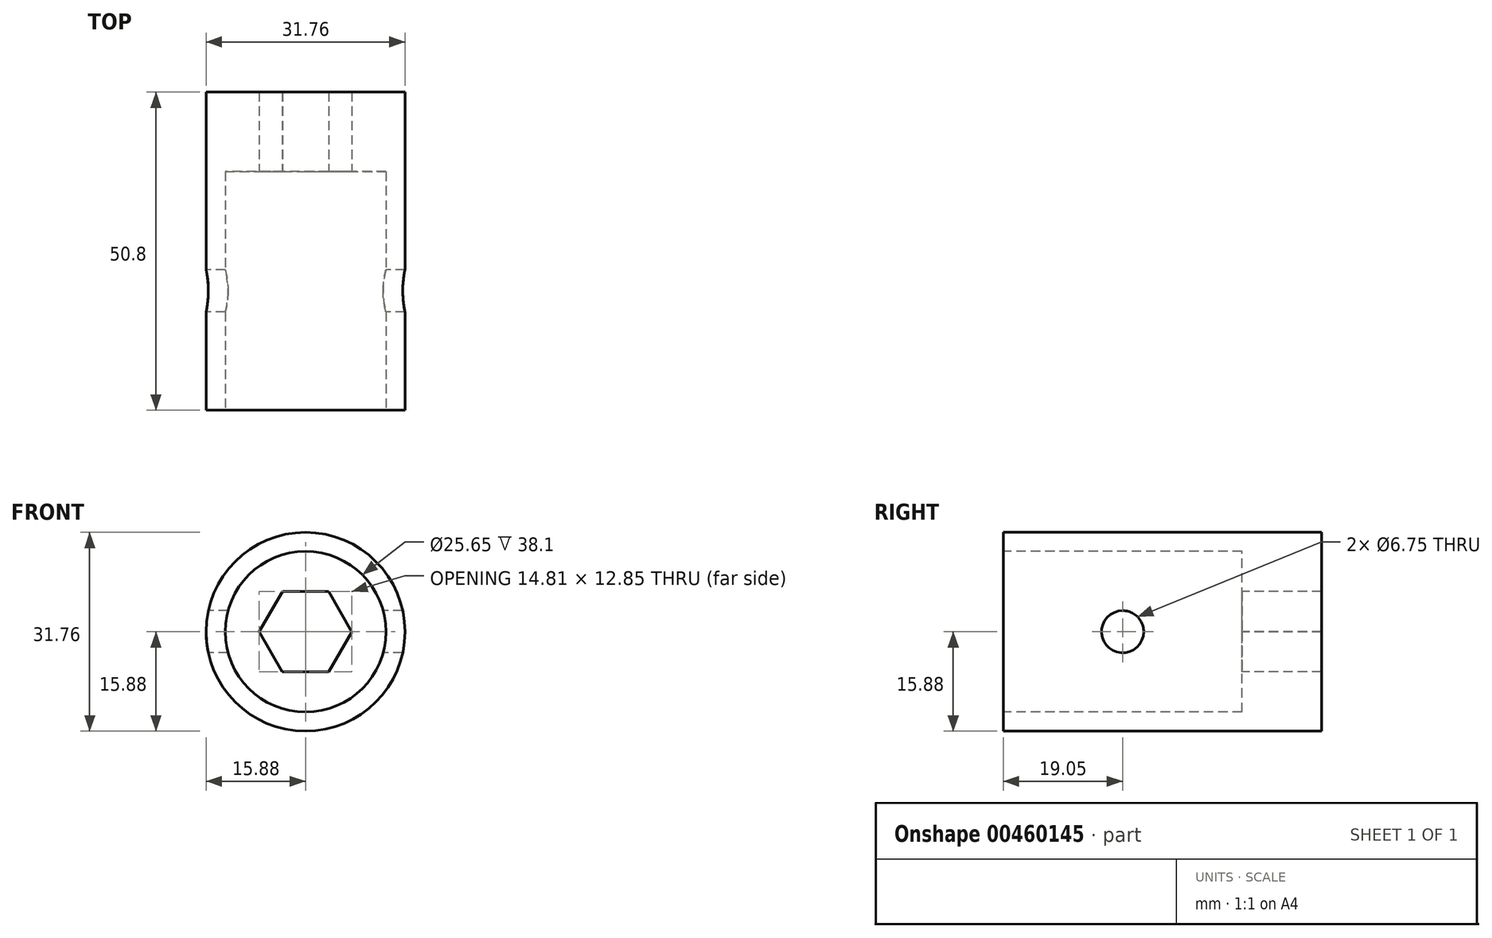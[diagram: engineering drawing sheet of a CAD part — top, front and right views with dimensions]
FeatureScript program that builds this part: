
annotation { "Feature Type Name" : "Feature", "Feature Type Description" : "" }
export const myFeature = defineFeature(function(context is Context, id is Id, definition is map)
    precondition{}
    {
        {
            var Q0;
            Q0=qCreatedBy(makeId("Front.planeOp"),FACE);
            var sketch = newSketch(context, id + "F0", { "sketchPlane" : qUnion([Q0])});
            skCircle(sketch, "E0", {"center": v(0, 0) * mm, "radius": 15.88 * mm});
            skSolve(sketch);
        }
        {
            var Q0;
            Q0=makeQuery(id+"F0.imprint","IMPRINT",FACE,{"disambiguationData":[TD([[makeQuery(id+"F0.imprint","IMPRINT",EDGE,{"derivedFrom":sQuery(id+"F0.wireOp",EDGE,"E0")}),1.0]])]});
            extrude(context, id + "F1", {"entities" : qUnion([Q0]), "depth" : 50.8 * mm, "offsetDistance" : 25.4 * mm});
        }
        {
            var Q0;
            Q0=makeQuery(id+"F1.opExtrude","CAP_FACE",FACE,{"disambiguationData":[OSD([sQuery(id+"F0.wireOp",EDGE,"E0")])],"isStart":false});
            var sketch = newSketch(context, id + "F2", { "sketchPlane" : qUnion([Q0])});
            skCircle(sketch, "E1", {"center": v(0, 0) * mm, "radius": 12.83 * mm});
            skSolve(sketch);
        }
        {
            var Q0;
            Q0=makeQuery(id+"F2.imprint","IMPRINT",FACE,{"disambiguationData":[TD([[makeQuery(id+"F2.imprint","IMPRINT",EDGE,{"derivedFrom":sQuery(id+"F2.wireOp",EDGE,"E1")}),1.0]])]});
            extrude(context, id + "F3", {"entities" : qUnion([Q0]), "operationType" : NewBodyOperationType.REMOVE, "oppositeDirection" : true, "depth" : 38.1 * mm, "offsetDistance" : 25.4 * mm});
        }
        {
            var Q0;
            Q0=makeQuery(id+"F3.boolean.opBoolean","COPY",FACE,{"derivedFrom":makeQuery(id+"F3.opExtrude","CAP_FACE",FACE,{"disambiguationData":[OSD([sQuery(id+"F2.wireOp",EDGE,"E1")])],"isStart":false})});
            var sketch = newSketch(context, id + "F4", { "sketchPlane" : qUnion([Q0])});
            skCircle(sketch, "E2.cCircle", {"center": v(0, 0) * mm, "radius": 6.41 * mm, "construction": true});
            skLineSegment(sketch, "E2.0", {"start": v(3.72, 6.4) * mm, "end": v(7.4, -0.02) * mm});
            skLineSegment(sketch, "E2.1", {"start": v(7.4, -0.02) * mm, "end": v(3.68, -6.42) * mm});
            skLineSegment(sketch, "E2.2", {"start": v(3.68, -6.42) * mm, "end": v(-3.72, -6.4) * mm});
            skLineSegment(sketch, "E2.3", {"start": v(-3.72, -6.4) * mm, "end": v(-7.4, 0.02) * mm});
            skLineSegment(sketch, "E2.4", {"start": v(-7.4, 0.02) * mm, "end": v(-3.68, 6.42) * mm});
            skLineSegment(sketch, "E2.5", {"start": v(-3.68, 6.42) * mm, "end": v(3.72, 6.4) * mm});
            skPoint(sketch, "E2.0.midPoint", {"position": v(5.56, 3.19) * mm});
            skSolve(sketch);
        }
        {
            var Q0;
            Q0=makeQuery(id+"F4.imprint","IMPRINT",FACE,{"disambiguationData":[TD([[makeQuery(id+"F4.imprint","IMPRINT",EDGE,{"derivedFrom":sQuery(id+"F4.wireOp",EDGE,"E2.0")}),-1.0]])]});
            extrude(context, id + "F5", {"entities" : qUnion([Q0]), "operationType" : NewBodyOperationType.REMOVE, "oppositeDirection" : true, "depth" : 12.7 * mm, "offsetDistance" : 25.4 * mm});
        }
        {
            var Q0;
            Q0=qCreatedBy(makeId("Right.planeOp"),FACE);
            var sketch = newSketch(context, id + "F6", { "sketchPlane" : qUnion([Q0])});
            skCircle(sketch, "E3", {"center": v(-31.75, 0) * mm, "radius": 3.37 * mm});
            skSolve(sketch);
        }
        {
            var Q0;
            Q0 = qSketchRegion(id + "F6", true);
            extrude(context, id + "F7", {"entities" : qUnion([Q0]), "operationType" : NewBodyOperationType.REMOVE, "endBound" : BoundingType.SYMMETRIC, "depth" : 31.75 * mm, "offsetDistance" : 25.4 * mm});
        }
    });
